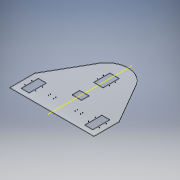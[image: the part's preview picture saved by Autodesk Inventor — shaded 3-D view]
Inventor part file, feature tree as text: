
AUTODESK INVENTOR PART (.ipt)
format: ipt  version: 2018 (Build 220112000, 112)  size: 234,496 bytes
history: native  units: in
note: dims shown in document units (in); Inventor stores cm internally (conversion verified against a paired STEP export)
features: extrude x2, sketch x2, plane x1, imported_body x1, projected_geometry x1
ambient origin geometry x8: Origin, YZ Plane, XZ Plane, XY Plane, X Axis, Y Axis, Z Axis, Center Point
bodies: Solid1 (feature_tree)
feature tree (7):
  extrude  "Extrusion2"  Depth=1.6142in
  plane  "Work Plane1"
  extrude  "Extrusion18"  TaperAngle=180.0deg  [1 undecoded]
  sketch  "Sketch3"  dims[d6=0.3937in d7=0.0in d64=1.6142in]
  sketch  "Sketch25"  dims[d67=14.175in d68=180.0deg d70=7.9055in d71=13.9849in d72=90.0deg d81=0.7874in d82=30.0deg d83=90.0deg d84=0.1969in d85=0.0in]
  imported_body  "Imported1"
  projected_geometry  "Project Cut Edges17"
note: 1 required parameter value undecoded (feature->parameter linkage not recoverable at this tier; creation-order binding heuristic only, values carry confidence <= 0.55)
